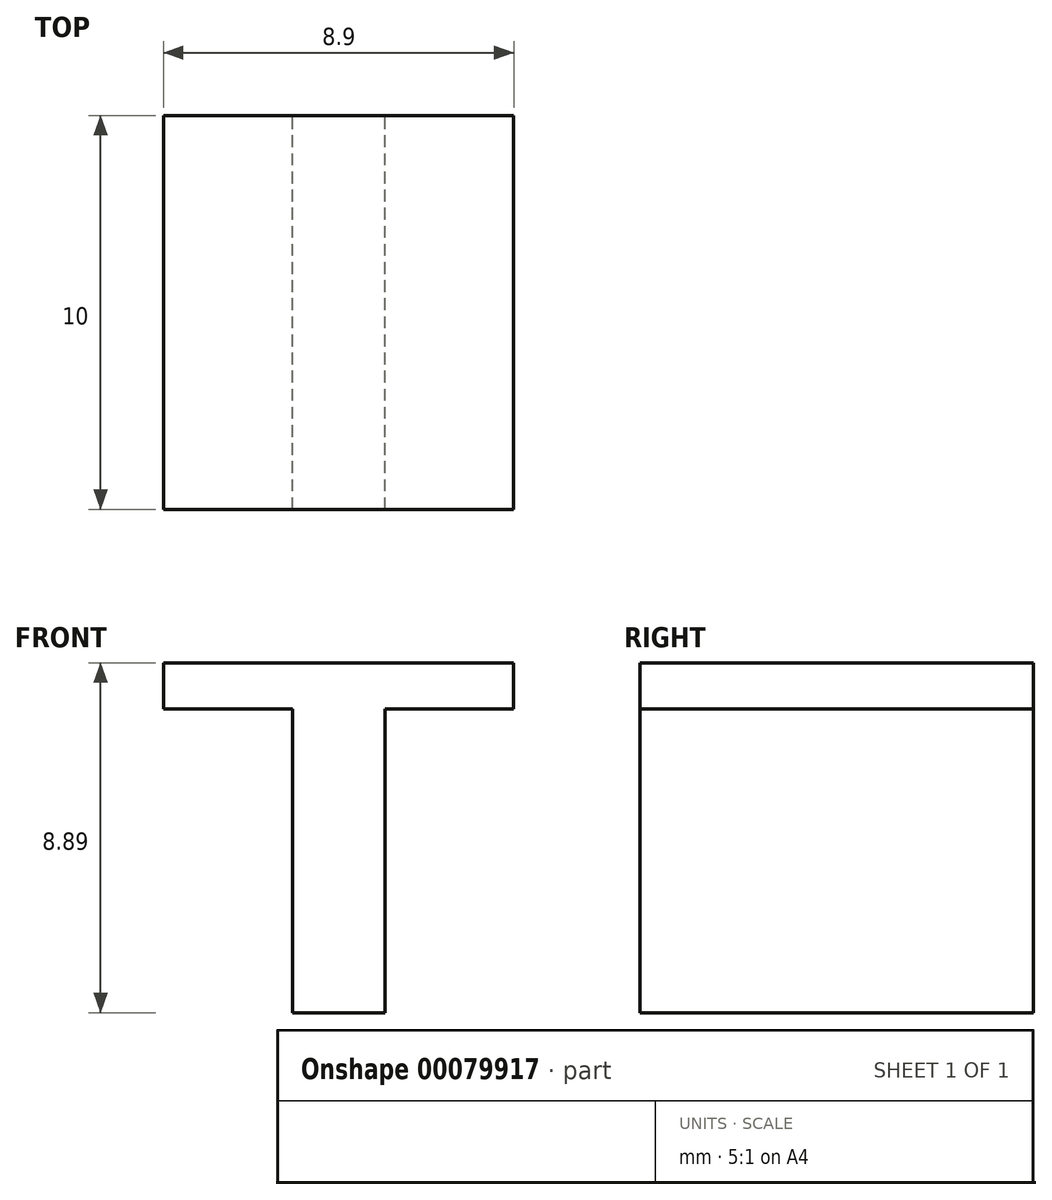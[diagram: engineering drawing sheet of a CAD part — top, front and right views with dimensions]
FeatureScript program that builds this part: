
annotation { "Feature Type Name" : "Feature", "Feature Type Description" : "" }
export const myFeature = defineFeature(function(context is Context, id is Id, definition is map)
    precondition{}
    {
        {
            var Q0;
            Q0=qCreatedBy(makeId("Front.planeOp"),FACE);
            var sketch = newSketch(context, id + "F0", { "sketchPlane" : qUnion([Q0])});
            skLineSegment(sketch, "E0.bottom", {"start": v(1.17, -4.15) * mm, "end": v(-1.17, -4.15) * mm});
            skLineSegment(sketch, "E0.top", {"start": v(1.17, 4.15) * mm, "end": v(-1.17, 4.15) * mm});
            skLineSegment(sketch, "E0.left", {"start": v(1.17, -4.15) * mm, "end": v(1.17, 4.15) * mm});
            skLineSegment(sketch, "E0.right", {"start": v(-1.17, -4.15) * mm, "end": v(-1.17, 4.15) * mm});
            skPoint(sketch, "E0.middle", {"position": v(0, 0) * mm});
            skLineSegment(sketch, "E1.bottom", {"start": v(4.45, 3.57) * mm, "end": v(-4.45, 3.57) * mm});
            skLineSegment(sketch, "E1.top", {"start": v(4.45, 4.74) * mm, "end": v(-4.45, 4.74) * mm});
            skLineSegment(sketch, "E1.left", {"start": v(4.45, 3.57) * mm, "end": v(4.45, 4.74) * mm});
            skLineSegment(sketch, "E1.right", {"start": v(-4.45, 3.57) * mm, "end": v(-4.45, 4.74) * mm});
            skPoint(sketch, "E1.middle", {"position": v(0, 4.15) * mm});
            skLineSegment(sketch, "E2.bottom", {"start": v(-1.37, 4.74) * mm, "end": v(1.12, 4.74) * mm});
            skLineSegment(sketch, "E3", {"start": v(-0.12, 21.25) * mm, "end": v(-1.37, 19.44) * mm});
            skLineSegment(sketch, "E4", {"start": v(-1.37, 19.44) * mm, "end": v(-0.12, 21.25) * mm});
            skLineSegment(sketch, "E5", {"start": v(-0.12, 21.25) * mm, "end": v(1.12, 19.44) * mm});
            skLineSegment(sketch, "E6", {"start": v(-1.37, 19.44) * mm, "end": v(-1.37, 4.74) * mm});
            skLineSegment(sketch, "E7", {"start": v(1.12, 4.74) * mm, "end": v(1.12, 19.44) * mm});
            skLineSegment(sketch, "E8", {"start": v(0, 4.74) * mm, "end": v(0, 13.1) * mm});
            skSolve(sketch);
        }
        {
            var Q0;
            Q0=makeQuery(id+"F0.imprint","IMPRINT",FACE,{"disambiguationData":[TD([[makeQuery(id+"F0.imprint","IMPRINT",EDGE,{"derivedFrom":sQuery(id+"F0.wireOp",EDGE,"E4")}),-1.0]])]});
            var Q1;
            {var subQ8=sQuery(id+"F0.wireOp",EDGE,"E0.top");Q1=makeQuery(id+"F0.imprint","IMPRINT",FACE,{"disambiguationData":[TD([[makeQuery(id+"F0.imprint","IMPRINT",EDGE,{"derivedFrom":subQ8}),-1.0]])]});}
            var Q2;
            {var subQ0=sQuery(id+"F0.wireOp",EDGE,"E0.bottom");Q2=makeQuery(id+"F0.imprint","IMPRINT",FACE,{"disambiguationData":[TD([[makeQuery(id+"F0.imprint","IMPRINT",EDGE,{"derivedFrom":subQ0}),-1.0]])]});}
            var Q3;
            {var subQ0=sQuery(id+"F0.wireOp",EDGE,"E0.top");Q3=makeQuery(id+"F0.imprint","IMPRINT",FACE,{"disambiguationData":[TD([[makeQuery(id+"F0.imprint","IMPRINT",EDGE,{"derivedFrom":subQ0}),1.0]])]});}
            extrude(context, id + "F1", {"entities" : qUnion([Q0, Q1, Q2, Q3]), "depth" : 10 * mm});
        }
    });
